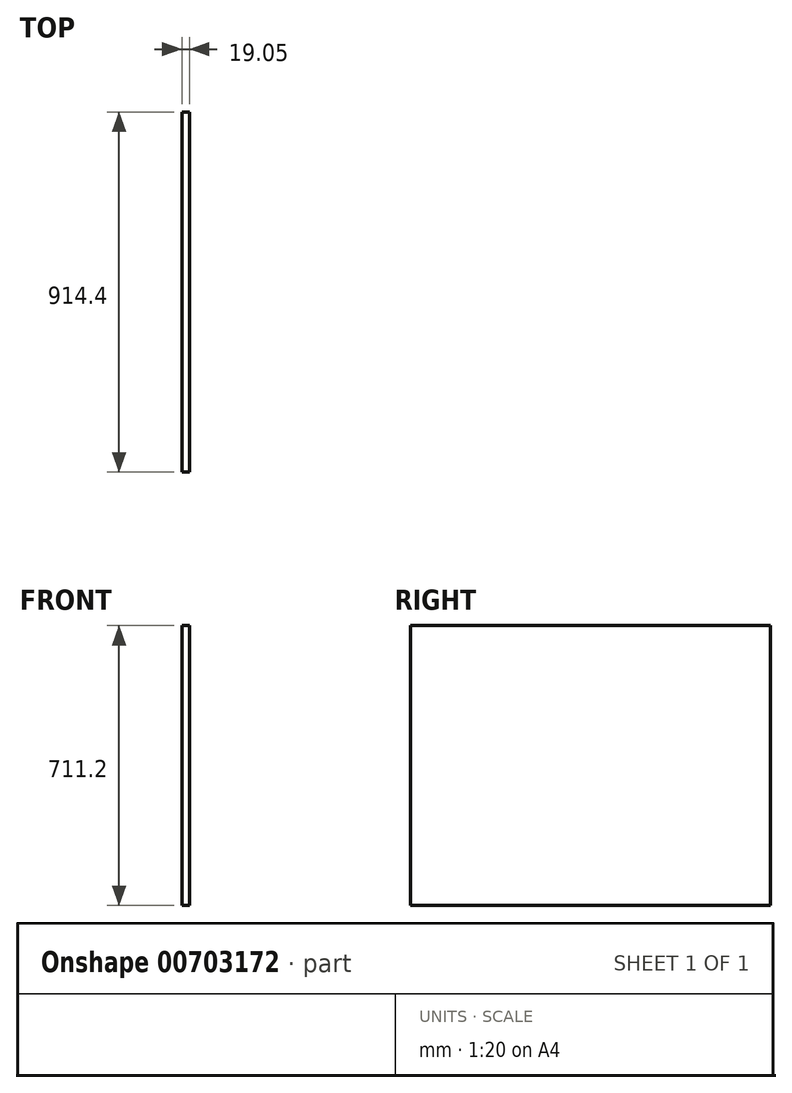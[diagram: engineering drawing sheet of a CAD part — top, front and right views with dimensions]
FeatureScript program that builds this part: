
annotation { "Feature Type Name" : "Feature", "Feature Type Description" : "" }
export const myFeature = defineFeature(function(context is Context, id is Id, definition is map)
    precondition{}
    {
        {
            var Q0;
            Q0=qCreatedBy(makeId("Right.planeOp"),FACE);
            var sketch = newSketch(context, id + "F0", { "sketchPlane" : qUnion([Q0])});
            skLineSegment(sketch, "E0.bottom", {"start": v(457.2, 355.6) * mm, "end": v(-457.2, 355.6) * mm});
            skLineSegment(sketch, "E0.top", {"start": v(457.2, -355.6) * mm, "end": v(-457.2, -355.6) * mm});
            skLineSegment(sketch, "E0.left", {"start": v(457.2, 355.6) * mm, "end": v(457.2, -355.6) * mm});
            skLineSegment(sketch, "E0.right", {"start": v(-457.2, 355.6) * mm, "end": v(-457.2, -355.6) * mm});
            skPoint(sketch, "E0.middle", {"position": v(0, 0) * mm});
            skSolve(sketch);
        }
        {
            var Q0;
            Q0=makeQuery(id+"F0.imprint","IMPRINT",FACE,{"disambiguationData":[TD([[makeQuery(id+"F0.imprint","IMPRINT",EDGE,{"derivedFrom":sQuery(id+"F0.wireOp",EDGE,"E0.bottom")}),1.0]])]});
            extrude(context, id + "F1", {"entities" : qUnion([Q0]), "depth" : 19.05 * mm, "offsetDistance" : 25.4 * mm});
        }
    });
